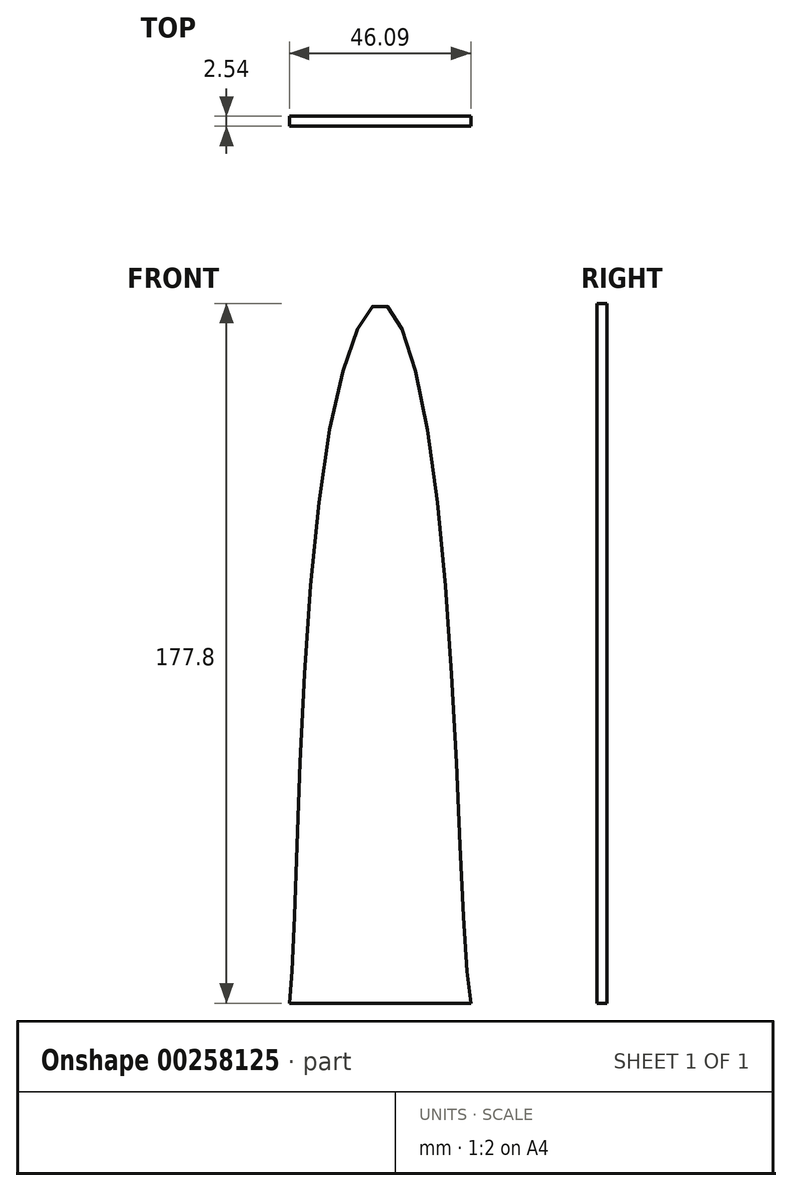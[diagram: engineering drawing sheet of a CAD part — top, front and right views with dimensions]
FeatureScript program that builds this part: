
annotation { "Feature Type Name" : "Feature", "Feature Type Description" : "" }
export const myFeature = defineFeature(function(context is Context, id is Id, definition is map)
    precondition{}
    {
        {
            var Q0;
            Q0=qCreatedBy(makeId("Front.planeOp"),FACE);
            var sketch = newSketch(context, id + "F0", { "sketchPlane" : qUnion([Q0])});
            skPoint(sketch, "E0", {"position": v(-15.61, 127) * mm});
            skPoint(sketch, "E1", {"position": v(14.62, 127) * mm});
            skPoint(sketch, "E2", {"position": v(23.05, 0) * mm});
            skPoint(sketch, "E3", {"position": v(-23.04, 0) * mm});
            skFitSpline(sketch, "E4", {"points": [v(-23.04, 0) * mm, v(-15.61, 127) * mm, v(0, 177.8) * mm, v(14.62, 127) * mm, v(23.05, 0) * mm], "startDerivative": vector(18.72, 111.42) * mm, "endDerivative": vector(25.02, -110.67) * mm});
            skLineSegment(sketch, "E5", {"start": v(-23.04, 0) * mm, "end": v(23.05, 0) * mm});
            skSolve(sketch);
        }
        {
            var Q0;
            Q0=makeQuery(id+"F0.imprint","IMPRINT",FACE,{"disambiguationData":[TD([[makeQuery(id+"F0.imprint","IMPRINT",EDGE,{"derivedFrom":sQuery(id+"F0.wireOp",EDGE,"E4")}),-1.0]])]});
            extrude(context, id + "F1", {"entities" : qUnion([Q0]), "depth" : 2.54 * mm});
        }
    });
